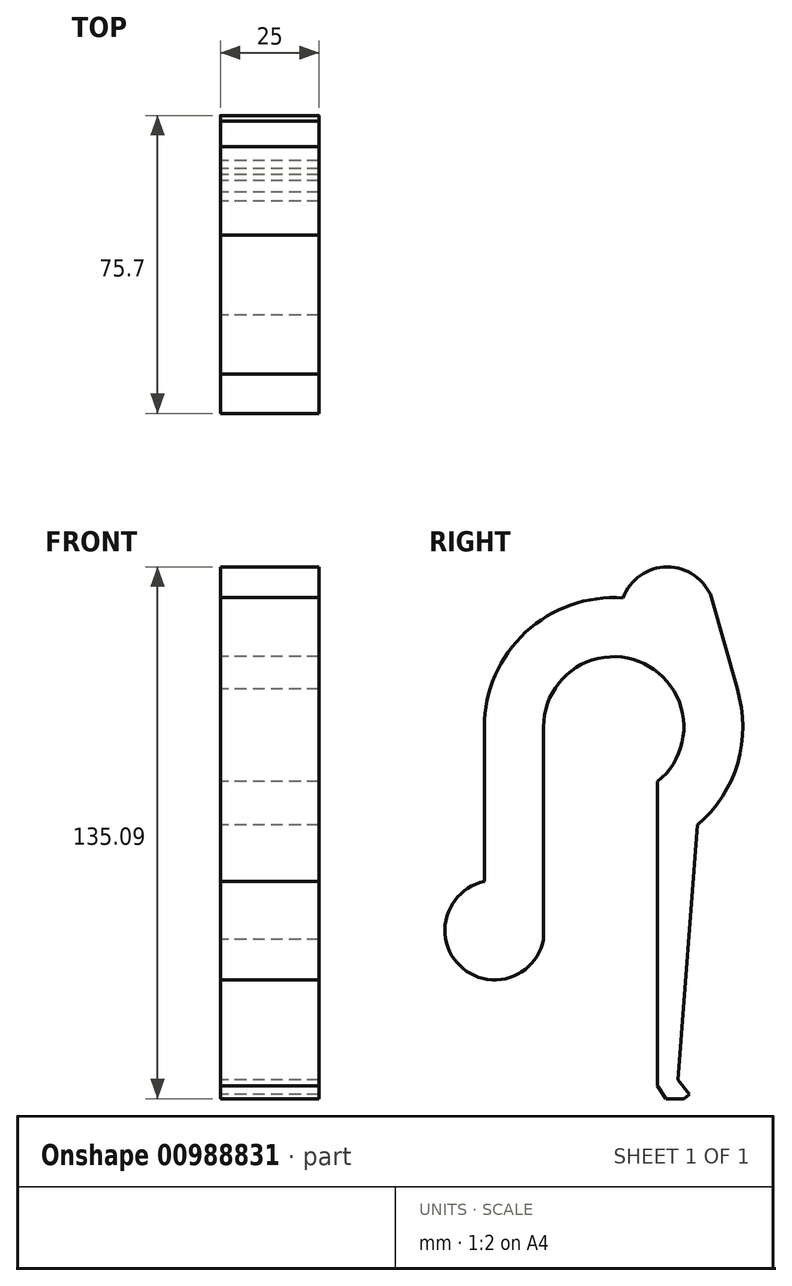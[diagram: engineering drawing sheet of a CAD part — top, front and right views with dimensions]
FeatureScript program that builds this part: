
annotation { "Feature Type Name" : "Feature", "Feature Type Description" : "" }
export const myFeature = defineFeature(function(context is Context, id is Id, definition is map)
    precondition{}
    {
        {
            var Q0;
            Q0=qCreatedBy(makeId("Right.planeOp"),FACE);
            var sketch = newSketch(context, id + "F0", { "sketchPlane" : qUnion([Q0])});
            skCircle(sketch, "E0", {"center": v(0, 0) * mm, "radius": 17.83 * mm});
            skCircle(sketch, "E1.0", {"center": v(0, 0) * mm, "radius": 32.83 * mm});
            skLineSegment(sketch, "E2.bottom", {"start": v(-17.83, 0) * mm, "end": v(11.14, 0) * mm});
            skLineSegment(sketch, "E2.top", {"start": v(-17.83, -91.25) * mm, "end": v(11.14, -91.25) * mm});
            skLineSegment(sketch, "E2.left", {"start": v(-17.83, 0) * mm, "end": v(-17.83, -91.25) * mm});
            skLineSegment(sketch, "E2.right", {"start": v(11.14, 0) * mm, "end": v(11.14, -91.25) * mm});
            skLineSegment(sketch, "E3.bottom", {"start": v(-32.83, 0) * mm, "end": v(-17.83, 0) * mm});
            skLineSegment(sketch, "E3.top", {"start": v(-32.83, -49.36) * mm, "end": v(-17.83, -49.36) * mm});
            skLineSegment(sketch, "E3.left", {"start": v(-32.83, 0) * mm, "end": v(-32.83, -49.36) * mm});
            skLineSegment(sketch, "E3.right", {"start": v(-17.83, 0) * mm, "end": v(-17.83, -49.36) * mm});
            skLineSegment(sketch, "E4.bottom", {"start": v(11.14, -91.25) * mm, "end": v(21.32, -91.25) * mm});
            skLineSegment(sketch, "E4.top", {"start": v(11.14, 0) * mm, "end": v(21.32, 0) * mm});
            skLineSegment(sketch, "E4.left", {"start": v(11.14, -91.25) * mm, "end": v(11.14, 0) * mm});
            skLineSegment(sketch, "E4.right", {"start": v(21.32, -91.25) * mm, "end": v(21.32, 0) * mm});
            skLineSegment(sketch, "E5", {"start": v(21.32, -24.96) * mm, "end": v(16.23, -91.25) * mm});
            skCircle(sketch, "E6", {"center": v(-30.24, -51.65) * mm, "radius": 12.63 * mm});
            skLineSegment(sketch, "E7", {"start": v(16.35, -89.62) * mm, "end": v(19.3, -93.3) * mm});
            skLineSegment(sketch, "E8", {"start": v(19.3, -93.3) * mm, "end": v(17.86, -94.46) * mm});
            skLineSegment(sketch, "E9", {"start": v(17.86, -94.46) * mm, "end": v(13.33, -94.46) * mm});
            skLineSegment(sketch, "E10", {"start": v(13.33, -94.46) * mm, "end": v(11.14, -91.25) * mm});
            skLineSegment(sketch, "E11", {"start": v(31.83, 8.04) * mm, "end": v(24.9, 32.83) * mm});
            skCircle(sketch, "E12", {"center": v(13.67, 28.64) * mm, "radius": 12 * mm});
            skSolve(sketch);
        }
        {
            var Q0;
            {var subQ5=sQuery(id+"F0.wireOp",EDGE,"E3.bottom");Q0=makeQuery(id+"F0.imprint","IMPRINT",FACE,{"disambiguationData":[TD([[makeQuery(id+"F0.imprint","IMPRINT",EDGE,{"derivedFrom":subQ5}),1.0]])]});}
            var Q1;
            {var subQ0=sQuery(id+"F0.wireOp",EDGE,"E3.bottom");Q1=makeQuery(id+"F0.imprint","IMPRINT",FACE,{"disambiguationData":[TD([[makeQuery(id+"F0.imprint","IMPRINT",EDGE,{"derivedFrom":subQ0}),-1.0]])]});}
            var Q2;
            {var subQ4=sQuery(id+"F0.wireOp",EDGE,"E3.top");Q2=makeQuery(id+"F0.imprint","IMPRINT",FACE,{"disambiguationData":[TD([[makeQuery(id+"F0.imprint","IMPRINT",EDGE,{"derivedFrom":subQ4}),1.0]])]});}
            var Q3;
            {var subQ0=sQuery(id+"F0.wireOp",EDGE,"fXLxpR4K-gr3u-5qwG-5c9m-b6GSeRlWyGYh.top");Q3=makeQuery(id+"F0.imprint","IMPRINT",FACE,{"disambiguationData":[TD([[makeQuery(id+"F0.imprint","IMPRINT",EDGE,{"derivedFrom":subQ0}),1.0]])]});}
            var Q4;
            {var subQ0=sQuery(id+"F0.wireOp",EDGE,"fXLxpR4K-gr3u-5qwG-5c9m-b6GSeRlWyGYh.right");var subQ1=sQuery(id+"F0.wireOp",EDGE,"E1.0");var subQ2=makeQuery(id+"F0.imprint","INTERSECT",VERTEX,{"derivedFrom":[subQ1,subQ0]});Q4=makeQuery(id+"F0.imprint","IMPRINT",FACE,{"disambiguationData":[TD([[makeQuery(id+"F0.imprint","IMPRINT",EDGE,{"disambiguationData":[TD([[subQ2,1.0]])],"derivedFrom":subQ1}),1.0]])]});}
            var Q5;
            {var subQ0=sQuery(id+"F0.wireOp",EDGE,"fXLxpR4K-gr3u-5qwG-5c9m-b6GSeRlWyGYh.left");var subQ1=sQuery(id+"F0.wireOp",EDGE,"E1.0");var subQ2=makeQuery(id+"F0.imprint","INTERSECT",VERTEX,{"derivedFrom":[subQ1,subQ0]});Q5=makeQuery(id+"F0.imprint","IMPRINT",FACE,{"disambiguationData":[TD([[makeQuery(id+"F0.imprint","IMPRINT",EDGE,{"disambiguationData":[TD([[subQ2,-1.0]])],"derivedFrom":subQ1}),-1.0]])]});}
            var Q6;
            {var subQ1=sQuery(id+"F0.wireOp",EDGE,"E0");var subQ7=sQuery(id+"F0.wireOp",EDGE,"E4.top");var subQ9=makeQuery(id+"F0.imprint","INTERSECT",VERTEX,{"derivedFrom":[subQ1,subQ7]});Q6=makeQuery(id+"F0.imprint","IMPRINT",FACE,{"disambiguationData":[TD([[makeQuery(id+"F0.imprint","IMPRINT",EDGE,{"disambiguationData":[TD([[subQ9,1.0]])],"derivedFrom":subQ1}),-1.0]])]});}
            var Q7;
            {var subQ1=sQuery(id+"F0.wireOp",EDGE,"E3.top");var subQ5=sQuery(id+"F0.wireOp",EDGE,"E6");var subQ6=makeQuery(id+"F0.imprint","INTERSECT",VERTEX,{"derivedFrom":[subQ1,subQ5]});Q7=makeQuery(id+"F0.imprint","IMPRINT",FACE,{"disambiguationData":[TD([[makeQuery(id+"F0.imprint","IMPRINT",EDGE,{"disambiguationData":[TD([[subQ6,-1.0]])],"derivedFrom":subQ5}),-1.0]])]});}
            var Q8;
            {var subQ0=sQuery(id+"F0.wireOp",EDGE,"E3.left");var subQ1=sQuery(id+"F0.wireOp",EDGE,"E3.top");var subQ2=makeQuery(id+"F0.imprint","INTERSECT",VERTEX,{"derivedFrom":[subQ1,subQ0]});Q8=makeQuery(id+"F0.imprint","IMPRINT",FACE,{"disambiguationData":[TD([[makeQuery(id+"F0.imprint","IMPRINT",EDGE,{"disambiguationData":[TD([[subQ2,-1.0]])],"derivedFrom":subQ1}),-1.0]])]});}
            var Q9;
            {var subQ1=sQuery(id+"F0.wireOp",EDGE,"E1.0");var subQ3=sQuery(id+"F0.wireOp",EDGE,"E3.right");var subQ4=makeQuery(id+"F0.imprint","INTERSECT",VERTEX,{"derivedFrom":[subQ1,subQ3]});Q9=makeQuery(id+"F0.imprint","IMPRINT",FACE,{"disambiguationData":[TD([[makeQuery(id+"F0.imprint","IMPRINT",EDGE,{"disambiguationData":[TD([[subQ4,-1.0]])],"derivedFrom":subQ3}),-1.0]])]});}
            var Q10;
            {var subQ4=sQuery(id+"F0.wireOp",EDGE,"E3.left");var subQ6=sQuery(id+"F0.wireOp",EDGE,"E3.top");var subQ7=makeQuery(id+"F0.imprint","INTERSECT",VERTEX,{"derivedFrom":[subQ6,subQ4]});Q10=makeQuery(id+"F0.imprint","IMPRINT",FACE,{"disambiguationData":[TD([[makeQuery(id+"F0.imprint","IMPRINT",EDGE,{"disambiguationData":[TD([[subQ7,-1.0]])],"derivedFrom":subQ6}),1.0]])]});}
            var Q11;
            {var subQ0=sQuery(id+"F0.wireOp",EDGE,"E5");var subQ1=sQuery(id+"F0.wireOp",EDGE,"E4.bottom");var subQ2=makeQuery(id+"F0.imprint","INTERSECT",VERTEX,{"derivedFrom":[subQ1,subQ0]});Q11=makeQuery(id+"F0.imprint","IMPRINT",FACE,{"disambiguationData":[TD([[makeQuery(id+"F0.imprint","IMPRINT",EDGE,{"disambiguationData":[TD([[subQ2,-1.0]])],"derivedFrom":subQ1}),1.0]])]});}
            var Q12;
            {var subQ0=sQuery(id+"F0.wireOp",EDGE,"E8");Q12=makeQuery(id+"F0.imprint","IMPRINT",FACE,{"disambiguationData":[TD([[makeQuery(id+"F0.imprint","IMPRINT",EDGE,{"derivedFrom":subQ0}),-1.0]])]});}
            var Q13;
            {var subQ0=sQuery(id+"F0.wireOp",EDGE,"E12");var subQ1=sQuery(id+"F0.wireOp",EDGE,"E1.0");var subQ2=makeQuery(id+"F0.imprint","INTERSECT",VERTEX,{"disambiguationData":[OD(0.0)],"derivedFrom":[subQ1,subQ0]});Q13=makeQuery(id+"F0.imprint","IMPRINT",FACE,{"disambiguationData":[TD([[makeQuery(id+"F0.imprint","IMPRINT",EDGE,{"disambiguationData":[TD([[subQ2,1.0]])],"derivedFrom":subQ1}),-1.0]])]});}
            var Q14;
            {var subQ0=sQuery(id+"F0.wireOp",EDGE,"E5");var subQ5=sQuery(id+"F0.wireOp",EDGE,"E4.bottom");var subQ8=makeQuery(id+"F0.imprint","INTERSECT",VERTEX,{"derivedFrom":[subQ5,subQ0]});Q14=makeQuery(id+"F0.imprint","IMPRINT",FACE,{"disambiguationData":[TD([[makeQuery(id+"F0.imprint","IMPRINT",EDGE,{"disambiguationData":[TD([[subQ8,1.0]])],"derivedFrom":subQ0}),-1.0]])]});}
            extrude(context, id + "F1", {"entities" : qUnion([Q0, Q1, Q2, Q3, Q4, Q5, Q6, Q7, Q8, Q9, Q10, Q11, Q12, Q13, Q14]), "depth" : 25 * mm, "offsetDistance" : 25 * mm});
        }
    });
